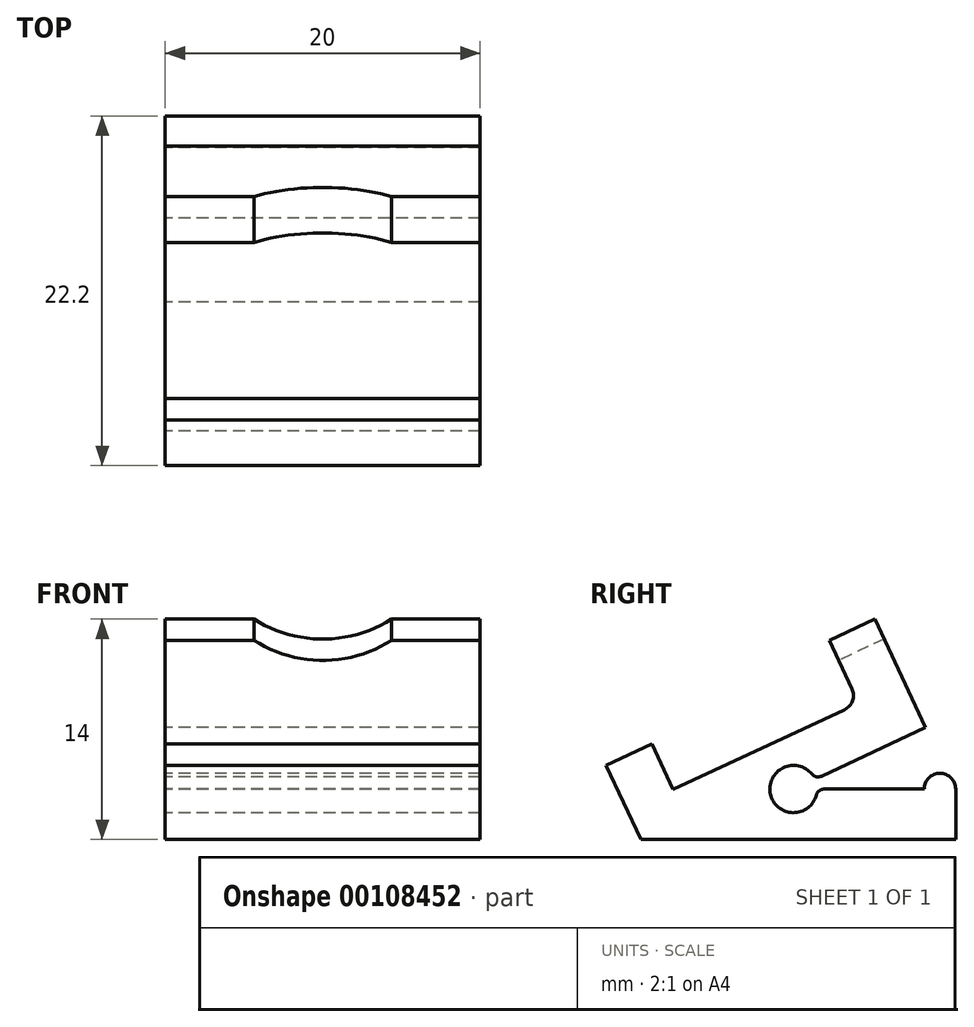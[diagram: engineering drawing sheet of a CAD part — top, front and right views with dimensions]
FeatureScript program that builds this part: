
annotation { "Feature Type Name" : "Feature", "Feature Type Description" : "" }
export const myFeature = defineFeature(function(context is Context, id is Id, definition is map)
    precondition{}
    {
        {
            var Q0;
            Q0=qCreatedBy(makeId("Right.planeOp"),FACE);
            var sketch = newSketch(context, id + "F0", { "sketchPlane" : qUnion([Q0])});
            skLineSegment(sketch, "E0", {"start": v(0, 0) * mm, "end": v(-2.2, 4.71) * mm});
            skLineSegment(sketch, "E1", {"start": v(-2.2, 4.71) * mm, "end": v(0.7, 6.07) * mm});
            skLineSegment(sketch, "E2", {"start": v(0.7, 6.07) * mm, "end": v(2.05, 3.16) * mm});
            skLineSegment(sketch, "E3", {"start": v(13.41, 9.57) * mm, "end": v(11.98, 12.65) * mm});
            skLineSegment(sketch, "E4", {"start": v(11.98, 12.65) * mm, "end": v(14.88, 14) * mm});
            skLineSegment(sketch, "E5", {"start": v(14.88, 14) * mm, "end": v(18.09, 7.11) * mm});
            skLineSegment(sketch, "E6", {"start": v(18.09, 7.11) * mm, "end": v(11.46, 4.02) * mm});
            skLineSegment(sketch, "E7", {"start": v(11.64, 3.2) * mm, "end": v(18, 3.2) * mm});
            skLineSegment(sketch, "E8", {"start": v(20, 3.2) * mm, "end": v(20, 0) * mm});
            skLineSegment(sketch, "E9", {"start": v(20, 0) * mm, "end": v(0, 0) * mm});
            skPoint(sketch, "E10.visualSharp", {"position": v(9.7, 3.2) * mm});
            skPoint(sketch, "E11.visualSharp", {"position": v(18.09, 7.11) * mm});
            skArc(sketch, "E12", {"start": v(20, 3.2) * mm, "mid": v(19, 4.2) * mm, "end": v(18, 3.2) * mm});
            skLineSegment(sketch, "E13", {"start": v(2.05, 3.16) * mm, "end": v(12.93, 8.24) * mm});
            skPoint(sketch, "E14.visualSharp", {"position": v(13.84, 8.66) * mm});
            skArc(sketch, "E14.filletArc", {"start": v(12.93, 8.24) * mm, "mid": v(13.45, 8.8) * mm, "end": v(13.41, 9.57) * mm});
            skArc(sketch, "E15", {"start": v(10.86, 4.15) * mm, "mid": v(8.24, 2.88) * mm, "end": v(11.15, 2.83) * mm});
            skPoint(sketch, "E16.visualSharp", {"position": v(11.06, 3.83) * mm});
            skArc(sketch, "E16.filletArc", {"start": v(10.86, 4.15) * mm, "mid": v(11.14, 3.98) * mm, "end": v(11.46, 4.02) * mm});
            skPoint(sketch, "E17.visualSharp", {"position": v(11.2, 3.2) * mm});
            skArc(sketch, "E17.filletArc", {"start": v(11.64, 3.2) * mm, "mid": v(11.33, 3.1) * mm, "end": v(11.15, 2.83) * mm});
            skSolve(sketch);
        }
        {
            var Q0;
            Q0 = qSketchRegion(id + "F0", true);
            extrude(context, id + "F1", {"entities" : qUnion([Q0]), "endBound" : BoundingType.SYMMETRIC, "depth" : 20 * mm});
        }
        {
            var Q0;
            Q0=makeQuery(id+"F1.opExtrude","SWEPT_FACE",FACE,{"disambiguationData":[OSD([sQuery(id+"F0.wireOp",EDGE,"E3")])]});
            var sketch = newSketch(context, id + "F2", { "sketchPlane" : qUnion([Q0])});
            skArc(sketch, "E18", {"start": v(-4.36, 6.4) * mm, "mid": v(0, 5) * mm, "end": v(4.36, 6.4) * mm});
            skLineSegment(sketch, "E19", {"start": v(-4.36, 6.4) * mm, "end": v(4.36, 6.4) * mm});
            skSolve(sketch);
        }
        {
            var Q0;
            Q0 = qSketchRegion(id + "F2", true);
            var Q1;
            Q1=makeQuery(id+"F1.opExtrude","SWEPT_FACE",FACE,{"disambiguationData":[OSD([sQuery(id+"F0.wireOp",EDGE,"E5")])]});
            extrude(context, id + "F3", {"entities" : qUnion([Q0]), "operationType" : NewBodyOperationType.REMOVE, "endBound" : BoundingType.UP_TO_SURFACE, "oppositeDirection" : true, "endBoundEntityFace" : qUnion([Q1]), "depth" : 25 * mm});
        }
    });
